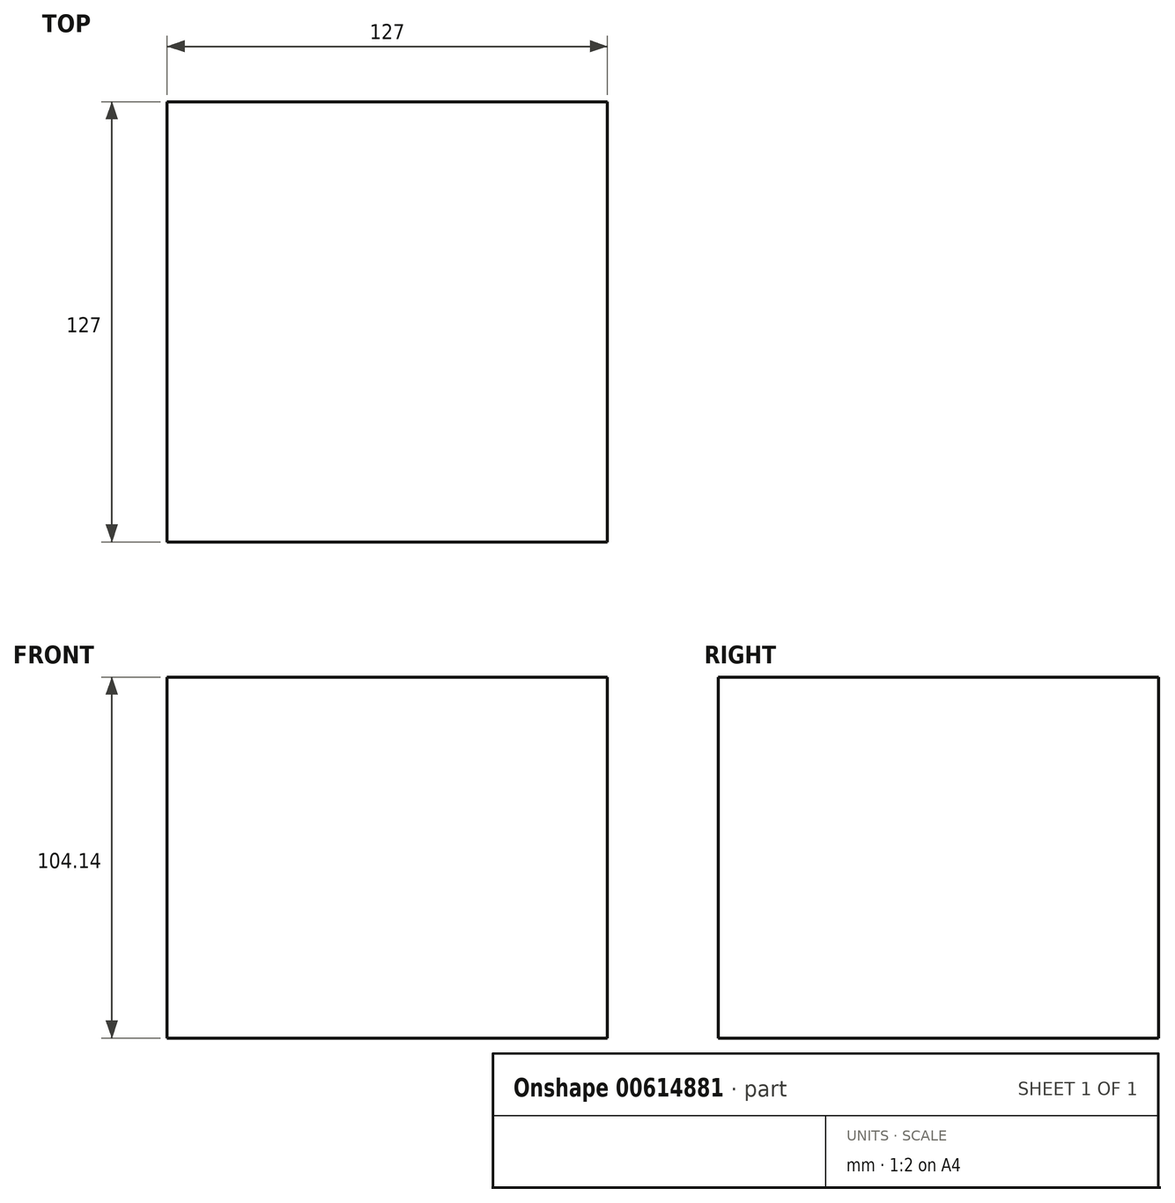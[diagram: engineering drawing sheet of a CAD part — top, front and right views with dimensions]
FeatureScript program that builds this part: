
annotation { "Feature Type Name" : "Feature", "Feature Type Description" : "" }
export const myFeature = defineFeature(function(context is Context, id is Id, definition is map)
    precondition{}
    {
        {
            var Q0;
            Q0=qCreatedBy(makeId("Top.planeOp"),FACE);
            var sketch = newSketch(context, id + "F0", { "sketchPlane" : qUnion([Q0])});
            skLineSegment(sketch, "E0.bottom", {"start": v(0, 0) * mm, "end": v(127, 0) * mm});
            skLineSegment(sketch, "E0.top", {"start": v(0, 127) * mm, "end": v(127, 127) * mm});
            skLineSegment(sketch, "E0.left", {"start": v(0, 0) * mm, "end": v(0, 127) * mm});
            skLineSegment(sketch, "E0.right", {"start": v(127, 0) * mm, "end": v(127, 127) * mm});
            skSolve(sketch);
        }
        {
            var Q0;
            Q0 = qSketchRegion(id + "F0", true);
            extrude(context, id + "F1", {"entities" : qUnion([Q0]), "depth" : 104.14 * mm, "offsetDistance" : 25.4 * mm});
        }
    });
